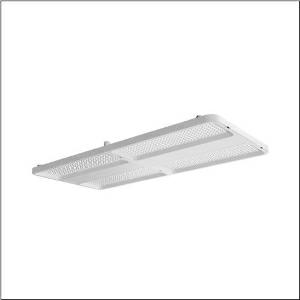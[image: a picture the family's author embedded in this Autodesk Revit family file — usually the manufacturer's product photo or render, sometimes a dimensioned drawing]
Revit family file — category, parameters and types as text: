
# Revit family: highbay_11_maxi_51hn11dbdlda
name_source: partatom
category: Lighting Fixtures
units: mm (PartAtom-declared; Revit-internal decimal feet)

## family parameters
Cut with Voids When Loaded = No
Host = Face
Light Source = No
Part Type = Normal
Room Calculation Point = No
Round Connector Dimension = Use Diameter
Shared = No

## types (1)
- --- (1 x LED, 4240 lm, 21.9 W, 4000K)
    Apparent Load = 22 VA
    CIE Flux Codes = 85 97 100 100 100
    Color Rendering = 90
    Color Temperature = 4000K
    Default Elevation = 1800 mm
    Description = high bay luminaire Highbay 11 maxi; direct symmetric narrow distribution, light control with lens of PMMA; UGR ≤ 19 (X = 4H | Y = 8H | S = 0.25H | reflection values 70/50/20); luminous flux: 26.600lm; light colour: 940, colour temperature: 4000K, MacAdam ≤ 2 SDCM (initial), colour rendering: CRI > 90; luminous efficacy: 181,7lm/W; rated service life: 100.000h (L95/B50) at AT= 25°C; control: DALI 2; luminaire connection: terminal, 5-pole, max. 2.5mm² (cable entry for one cable, Ø 8.5..16mm); mains connection: 230..240V, AC/DC 0/50..60Hz; connected load: 146,4W; protection rating (complete): IP66; insulation class (complete): insulation class I (protective earthing); protection symbol: D; impact resistance: IK08; certification: CE, ENEC, VDE, UKCA; luminaire for central battery installations according to DIN EN 60598-2-22, internal wiring halogen-free; luminaire LABS conformity tested according to VDMA 24364:2018-05; corresponds to IFS (International Featured Standards) requirements for safety and quality in the food industry; housing frame of high-performance plastic PA6, matt traffic white (RAL 9016); cover of PMMA; dimension (LxWxH): 946 x 442 x 72mm; permissible operating ambient temperature: -40..+60°C (reducing of maximum allowable ambient temperature of 5°C with ceiling mounting); packaging unit: 1 piece; (delivery without accessories; please order mounting accessories separately)
    Height = 72 mm  [stored 0.23622 ft]
    Lamp = 1 x LED
    Lamp Light Flux = 4240 lm
    Lamp Power = 21.9 W
    Lamp count = 1
    Length = 946 mm
    Luminous efficacy = 194 lm/W
    Manufacturer = Siteco
    ModVariant = No
    Model = 51HN11DBDLDA
    Mounting Place = Ceiling
    Mounting Type = Pendant
    Number of Poles = 1
    OnlyDefault = Yes
    Power Factor = 1
    Product Name = Highbay 11 maxi
    Product group = high bay luminaire
    ProductGroupID = 901
    Protection Class = Protection class I
    Protection Degree = IP 66
    RLX_Detail_Level = 1
    RLX_Emergency_Light_Flux = 0 lm
    RLX_Emergency_Type = 0
    RLX_Emergency_Type_DB = No
    RlxData = <blob elided: 127629 chars, md5=cc4e554f>
    Socket = socket
    Standby Power = 0 W
    System Light Flux = 4240 lm
    System Power = 22 W
    Type Comments = : DC mode (central or group accumulator) initial emergency light level
    Type Image = l_1363244.jpg
    URL = http://relux.com
    VarID = @adj_000353
    Voltage = 0 V
    Weight = 0.00 kg
    Width = 442 mm

note: [stored X ft] marks values corroborated as IEEE doubles in the binary element streams (Revit-internal decimal feet)

## geometry (parser evidence)
native form markers: Blend x4, Sweep x13
no freeform markers — native parametric forms only
